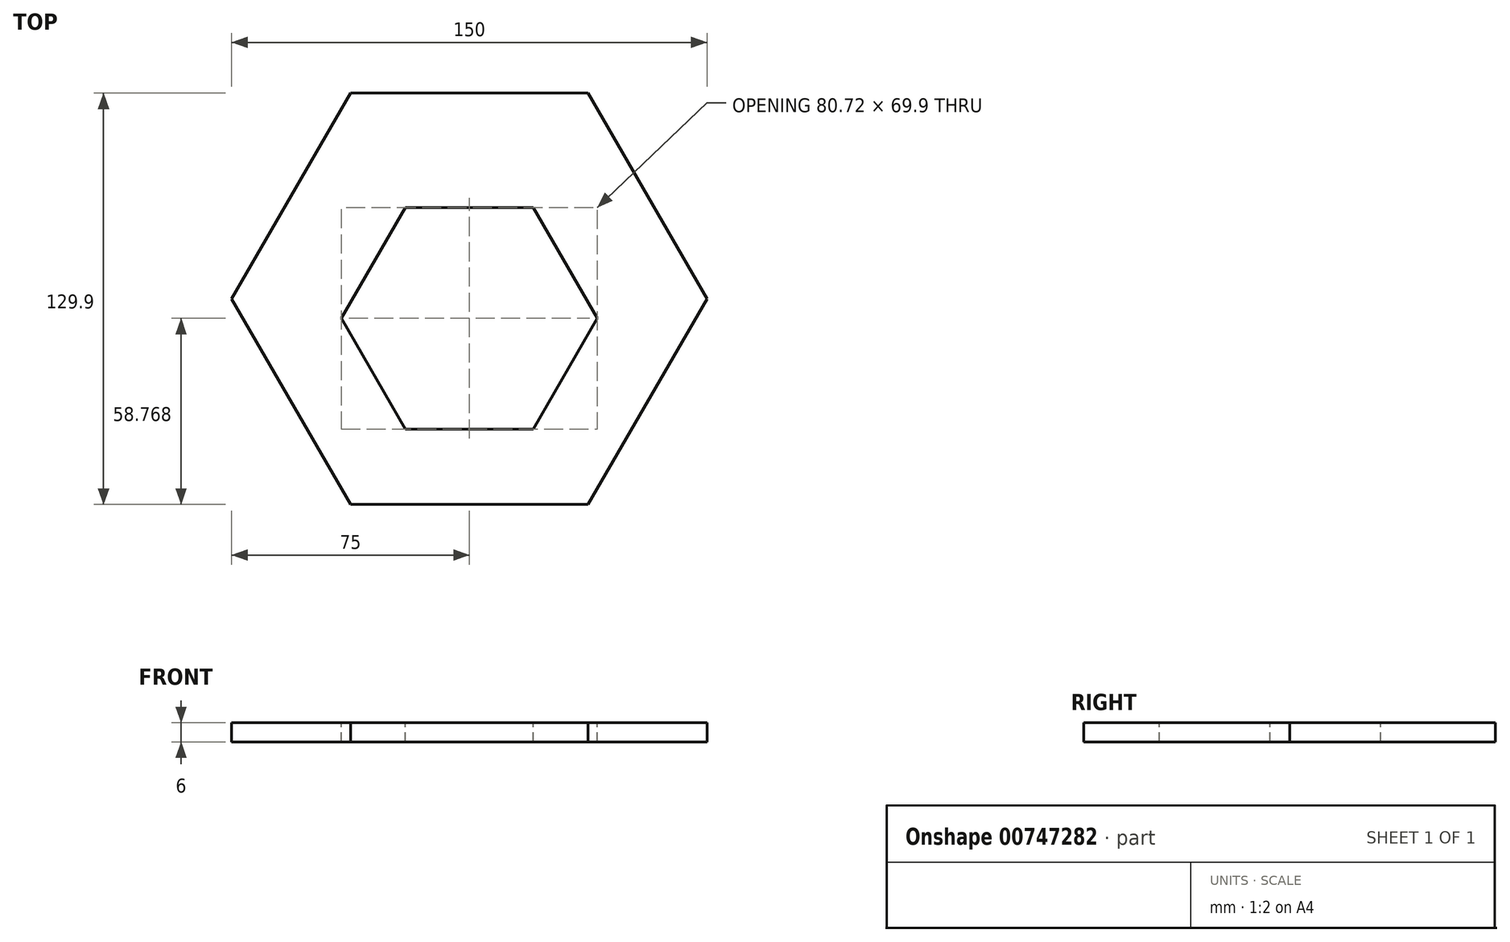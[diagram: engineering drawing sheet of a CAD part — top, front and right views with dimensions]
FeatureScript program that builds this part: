
annotation { "Feature Type Name" : "Feature", "Feature Type Description" : "" }
export const myFeature = defineFeature(function(context is Context, id is Id, definition is map)
    precondition{}
    {
        {
            var Q0;
            Q0=qCreatedBy(makeId("Top.planeOp"),FACE);
            var sketch = newSketch(context, id + "F0", { "sketchPlane" : qUnion([Q0])});
            skCircle(sketch, "E0.cCircle", {"center": v(0, 0) * mm, "radius": 64.95 * mm, "construction": true});
            skLineSegment(sketch, "E0.0", {"start": v(37.5, 64.95) * mm, "end": v(75, 0) * mm});
            skLineSegment(sketch, "E0.1", {"start": v(75, 0) * mm, "end": v(37.5, -64.95) * mm});
            skLineSegment(sketch, "E0.2", {"start": v(37.5, -64.95) * mm, "end": v(-37.5, -64.95) * mm});
            skLineSegment(sketch, "E0.3", {"start": v(-37.5, -64.95) * mm, "end": v(-75, 0) * mm});
            skLineSegment(sketch, "E0.4", {"start": v(-75, 0) * mm, "end": v(-37.5, 64.95) * mm});
            skLineSegment(sketch, "E0.5", {"start": v(-37.5, 64.95) * mm, "end": v(37.5, 64.95) * mm});
            skPoint(sketch, "E0.0.midPoint", {"position": v(64.95, 0) * mm});
            skSolve(sketch);
        }
        {
            var Q0;
            Q0=qSketchRegion(id+"F0",true);
            extrude(context, id + "F1", {"entities" : qUnion([Q0]), "depth" : 6 * mm, "offsetDistance" : 25 * mm});
        }
        {
            var Q0;
            Q0=makeQuery(id+"F1.opExtrude","CAP_FACE",FACE,{"disambiguationData":[OSD([sQuery(id+"F0.wireOp",EDGE,"E0.0"),sQuery(id+"F0.wireOp",EDGE,"E0.1"),sQuery(id+"F0.wireOp",EDGE,"E0.2"),sQuery(id+"F0.wireOp",EDGE,"E0.3"),sQuery(id+"F0.wireOp",EDGE,"E0.4"),sQuery(id+"F0.wireOp",EDGE,"E0.5")])],"isStart":false});
            var sketch = newSketch(context, id + "F2", { "sketchPlane" : qUnion([Q0])});
            skCircle(sketch, "E1.cCircle", {"center": v(0, -6.18) * mm, "radius": 34.95 * mm, "construction": true});
            skLineSegment(sketch, "E1.0", {"start": v(20.18, 28.77) * mm, "end": v(40.36, -6.18) * mm});
            skLineSegment(sketch, "E1.1", {"start": v(40.36, -6.18) * mm, "end": v(20.18, -41.13) * mm});
            skLineSegment(sketch, "E1.2", {"start": v(20.18, -41.13) * mm, "end": v(-20.18, -41.13) * mm});
            skLineSegment(sketch, "E1.3", {"start": v(-20.18, -41.13) * mm, "end": v(-40.36, -6.18) * mm});
            skLineSegment(sketch, "E1.4", {"start": v(-40.36, -6.18) * mm, "end": v(-20.18, 28.77) * mm});
            skLineSegment(sketch, "E1.5", {"start": v(-20.18, 28.77) * mm, "end": v(20.18, 28.77) * mm});
            skPoint(sketch, "E1.0.midPoint", {"position": v(30.27, 11.3) * mm});
            skSolve(sketch);
        }
        {
            var Q0;
            Q0=qSketchRegion(id+"F2",true);
            var Q1;
            Q1=makeQuery(id+"F1.opExtrude","CAP_FACE",FACE,{"disambiguationData":[OSD([sQuery(id+"F0.wireOp",EDGE,"E0.0"),sQuery(id+"F0.wireOp",EDGE,"E0.1"),sQuery(id+"F0.wireOp",EDGE,"E0.2"),sQuery(id+"F0.wireOp",EDGE,"E0.3"),sQuery(id+"F0.wireOp",EDGE,"E0.4"),sQuery(id+"F0.wireOp",EDGE,"E0.5")])],"isStart":true});
            extrude(context, id + "F3", {"entities" : qUnion([Q0]), "operationType" : NewBodyOperationType.REMOVE, "endBound" : BoundingType.UP_TO_SURFACE, "oppositeDirection" : true, "depth" : 25 * mm, "endBoundEntityFace" : qUnion([Q1]), "offsetDistance" : 25 * mm});
        }
    });
